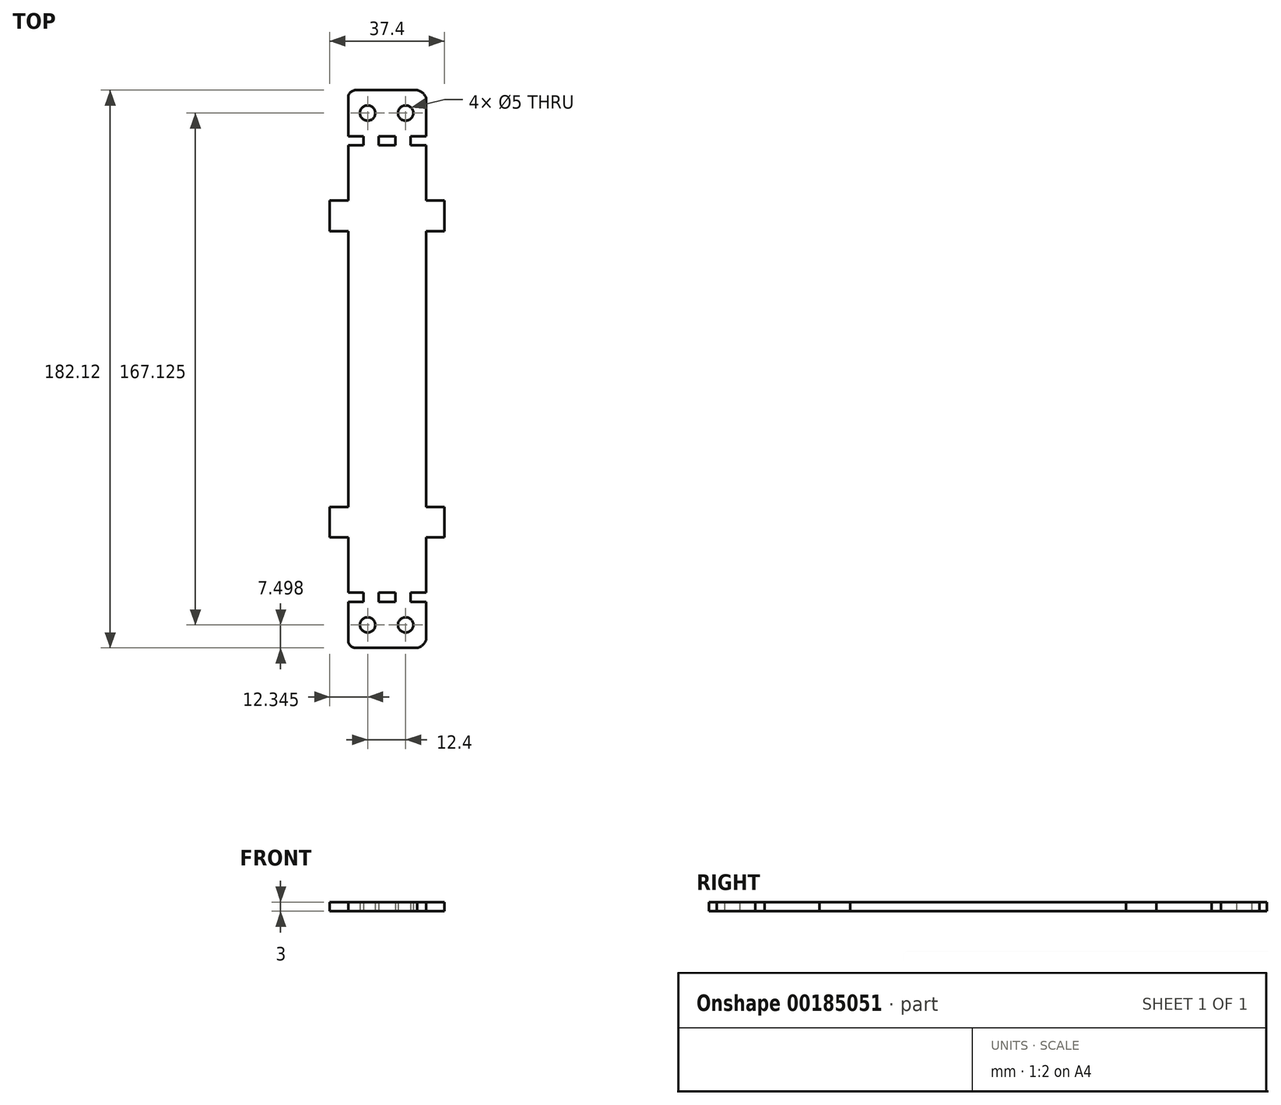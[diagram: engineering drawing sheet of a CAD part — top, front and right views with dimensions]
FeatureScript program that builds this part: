
annotation { "Feature Type Name" : "Feature", "Feature Type Description" : "" }
export const myFeature = defineFeature(function(context is Context, id is Id, definition is map)
    precondition{}
    {
        {
            var Q0;
            Q0=qCreatedBy(makeId("Top.planeOp"),FACE);
            var sketch = newSketch(context, id + "F0", { "sketchPlane" : qUnion([Q0])});
            skLineSegment(sketch, "E0", {"start": v(0, 91) * mm, "end": v(-10, 91) * mm});
            skLineSegment(sketch, "E1", {"start": v(-12.5, 76) * mm, "end": v(-9.5, 76) * mm});
            skLineSegment(sketch, "E2", {"start": v(-9.5, 76) * mm, "end": v(-9.5, 73) * mm});
            skLineSegment(sketch, "E3", {"start": v(-9.5, 73) * mm, "end": v(-12.5, 73) * mm});
            skLineSegment(sketch, "E4", {"start": v(-12.5, 88.5) * mm, "end": v(-12.5, 76) * mm});
            skLineSegment(sketch, "E5", {"start": v(0, 76) * mm, "end": v(-3, 76) * mm});
            skLineSegment(sketch, "E6", {"start": v(-3, 76) * mm, "end": v(-3, 73) * mm});
            skLineSegment(sketch, "E7", {"start": v(-3, 73) * mm, "end": v(0, 73) * mm});
            skCircle(sketch, "E8", {"center": v(-6.25, 83.5) * mm, "radius": 2.5 * mm});
            skPoint(sketch, "E8.centerSnap0", {"position": v(-12.5, 83.5) * mm});
            skPoint(sketch, "E8.centerSnap1", {"position": v(-6.25, 91) * mm});
            skPoint(sketch, "E9.visualSharp", {"position": v(-12.5, 91) * mm});
            skArc(sketch, "E9.filletArc", {"start": v(-10, 91) * mm, "mid": v(-11.77, 90.27) * mm, "end": v(-12.5, 88.5) * mm});
            skLineSegment(sketch, "E10", {"start": v(-12.5, 35) * mm, "end": v(-17.84, 35) * mm});
            skLineSegment(sketch, "E11", {"start": v(-18.5, 35.66) * mm, "end": v(-18.5, 44.34) * mm});
            skLineSegment(sketch, "E12", {"start": v(-17.84, 45) * mm, "end": v(-12.5, 45) * mm});
            skLineSegment(sketch, "E13", {"start": v(-12.5, 45) * mm, "end": v(-12.5, 73) * mm});
            skLineSegment(sketch, "E14", {"start": v(-12.5, 35) * mm, "end": v(-12.5, 0) * mm});
            skPoint(sketch, "E15.visualSharp", {"position": v(-18.5, 45) * mm});
            skArc(sketch, "E15.filletArc", {"start": v(-17.84, 45) * mm, "mid": v(-18.3, 44.8) * mm, "end": v(-18.5, 44.34) * mm});
            skPoint(sketch, "E16.visualSharp", {"position": v(-18.5, 35) * mm});
            skArc(sketch, "E16.filletArc", {"start": v(-18.5, 35.66) * mm, "mid": v(-18.3, 35.2) * mm, "end": v(-17.84, 35) * mm});
            skArc(sketch, "E17.MirrorCS", {"start": v(10, 91) * mm, "mid": v(11.77, 90.27) * mm, "end": v(12.5, 88.5) * mm});
            skLineSegment(sketch, "E18.MirrorCS", {"start": v(9.5, 76) * mm, "end": v(9.5, 73) * mm});
            skLineSegment(sketch, "E19.MirrorCS", {"start": v(9.5, 73) * mm, "end": v(12.5, 73) * mm});
            skLineSegment(sketch, "E20.MirrorCS", {"start": v(3, 76) * mm, "end": v(3, 73) * mm});
            skLineSegment(sketch, "E21.MirrorCS", {"start": v(12.5, 76) * mm, "end": v(9.5, 76) * mm});
            skLineSegment(sketch, "E22.MirrorCS", {"start": v(12.5, 35) * mm, "end": v(17.84, 35) * mm});
            skLineSegment(sketch, "E23.MirrorCS", {"start": v(17.84, 45) * mm, "end": v(12.5, 45) * mm});
            skLineSegment(sketch, "E24.MirrorCS", {"start": v(3, 73) * mm, "end": v(0, 73) * mm});
            skLineSegment(sketch, "E25.MirrorCS", {"start": v(0, 76) * mm, "end": v(3, 76) * mm});
            skPoint(sketch, "E26.MirrorP", {"position": v(6.25, 91) * mm});
            skCircle(sketch, "E27.MirrorC", {"center": v(6.25, 83.5) * mm, "radius": 2.5 * mm});
            skLineSegment(sketch, "E28.MirrorCS", {"start": v(0, 91) * mm, "end": v(10, 91) * mm});
            skLineSegment(sketch, "E29.MirrorCS", {"start": v(12.5, 45) * mm, "end": v(12.5, 73) * mm});
            skLineSegment(sketch, "E30.MirrorCS", {"start": v(12.5, 35) * mm, "end": v(12.5, 0) * mm});
            skLineSegment(sketch, "E31.MirrorCS", {"start": v(12.5, 88.5) * mm, "end": v(12.5, 76) * mm});
            skArc(sketch, "E32.MirrorCS", {"start": v(-17.84, -45) * mm, "mid": v(-18.3, -44.8) * mm, "end": v(-18.5, -44.34) * mm});
            skArc(sketch, "E33.MirrorCS", {"start": v(17.84, -45) * mm, "mid": v(18.3, -44.8) * mm, "end": v(18.5, -44.34) * mm});
            skArc(sketch, "E34.MirrorCS", {"start": v(-18.5, -35.66) * mm, "mid": v(-18.3, -35.2) * mm, "end": v(-17.84, -35) * mm});
            skArc(sketch, "E35.MirrorCS", {"start": v(-10, -91) * mm, "mid": v(-11.77, -90.27) * mm, "end": v(-12.5, -88.5) * mm});
            skArc(sketch, "E36.MirrorCS", {"start": v(32.1, -123.66) * mm, "mid": v(31.9, -123.2) * mm, "end": v(31.44, -123) * mm});
            skArc(sketch, "E37.MirrorCS", {"start": v(10, -91) * mm, "mid": v(11.77, -90.27) * mm, "end": v(12.5, -88.5) * mm});
            skLineSegment(sketch, "E38.MirrorCS", {"start": v(-17.84, -45) * mm, "end": v(-12.5, -45) * mm});
            skLineSegment(sketch, "E39.MirrorCS", {"start": v(9.5, -76) * mm, "end": v(9.5, -73) * mm});
            skLineSegment(sketch, "E40.MirrorCS", {"start": v(12.5, -76) * mm, "end": v(9.5, -76) * mm});
            skLineSegment(sketch, "E41.MirrorCS", {"start": v(3, -73) * mm, "end": v(0, -73) * mm});
            skLineSegment(sketch, "E42.MirrorCS", {"start": v(12.5, -35) * mm, "end": v(17.84, -35) * mm});
            skLineSegment(sketch, "E43.MirrorCS", {"start": v(3, -76) * mm, "end": v(3, -73) * mm});
            skLineSegment(sketch, "E44.MirrorCS", {"start": v(17.84, -45) * mm, "end": v(12.5, -45) * mm});
            skLineSegment(sketch, "E45.MirrorCS", {"start": v(-9.5, -73) * mm, "end": v(-12.5, -73) * mm});
            skLineSegment(sketch, "E46.MirrorCS", {"start": v(0, -76) * mm, "end": v(3, -76) * mm});
            skLineSegment(sketch, "E47.MirrorCS", {"start": v(-12.5, -76) * mm, "end": v(-9.5, -76) * mm});
            skLineSegment(sketch, "E48.MirrorCS", {"start": v(-9.5, -76) * mm, "end": v(-9.5, -73) * mm});
            skLineSegment(sketch, "E49.MirrorCS", {"start": v(0, -76) * mm, "end": v(-3, -76) * mm});
            skLineSegment(sketch, "E50.MirrorCS", {"start": v(-3, -76) * mm, "end": v(-3, -73) * mm});
            skLineSegment(sketch, "E51.MirrorCS", {"start": v(-3, -73) * mm, "end": v(0, -73) * mm});
            skLineSegment(sketch, "E52.MirrorCS", {"start": v(9.5, -73) * mm, "end": v(12.5, -73) * mm});
            skLineSegment(sketch, "E53.MirrorCS", {"start": v(-12.5, -35) * mm, "end": v(-17.84, -35) * mm});
            skLineSegment(sketch, "E54.MirrorCS", {"start": v(0, -91) * mm, "end": v(10, -91) * mm});
            skLineSegment(sketch, "E55.MirrorCS", {"start": v(-18.5, -35.66) * mm, "end": v(-18.5, -44.34) * mm});
            skLineSegment(sketch, "E56.MirrorCS", {"start": v(12.5, -88.5) * mm, "end": v(12.5, -76) * mm});
            skPoint(sketch, "E57.MirrorP", {"position": v(-12.5, -83.5) * mm});
            skPoint(sketch, "E58.MirrorP", {"position": v(-12.5, -91) * mm});
            skLineSegment(sketch, "E59.MirrorCS", {"start": v(18.5, -35.66) * mm, "end": v(18.5, -44.34) * mm});
            skPoint(sketch, "E60.MirrorP", {"position": v(-18.5, -45) * mm});
            skPoint(sketch, "E61.MirrorP", {"position": v(12.5, -91) * mm});
            skPoint(sketch, "E62.MirrorP", {"position": v(-6.25, -91) * mm});
            skCircle(sketch, "E63.MirrorC", {"center": v(6.25, -83.5) * mm, "radius": 2.5 * mm});
            skLineSegment(sketch, "E64.MirrorCS", {"start": v(-12.5, -88.5) * mm, "end": v(-12.5, -76) * mm});
            skLineSegment(sketch, "E65.MirrorCS", {"start": v(0, -91) * mm, "end": v(-10, -91) * mm});
            skLineSegment(sketch, "E66.MirrorCS", {"start": v(-12.5, -35) * mm, "end": v(-12.5, 0) * mm});
            skPoint(sketch, "E67.MirrorP", {"position": v(12.5, -83.5) * mm});
            skCircle(sketch, "E68.MirrorC", {"center": v(-6.25, -83.5) * mm, "radius": 2.5 * mm});
            skLineSegment(sketch, "E69.MirrorCS", {"start": v(-12.5, -45) * mm, "end": v(-12.5, -73) * mm});
            skLineSegment(sketch, "E70.MirrorCS", {"start": v(12.5, -35) * mm, "end": v(12.5, 0) * mm});
            skPoint(sketch, "E71.MirrorP", {"position": v(-18.5, -35) * mm});
            skLineSegment(sketch, "E72.MirrorCS", {"start": v(12.5, -45) * mm, "end": v(12.5, -73) * mm});
            skPoint(sketch, "E73.MirrorP", {"position": v(32.1, -123) * mm});
            skPoint(sketch, "E74.MirrorP", {"position": v(6.25, -91) * mm});
            skLineSegment(sketch, "E75", {"start": v(35.48, 76) * mm, "end": v(40.48, 76) * mm});
            skLineSegment(sketch, "E76", {"start": v(40.48, 76) * mm, "end": v(40.48, 73) * mm});
            skLineSegment(sketch, "E77", {"start": v(40.48, 73) * mm, "end": v(35.48, 73) * mm});
            skLineSegment(sketch, "E78", {"start": v(35.48, 88.56) * mm, "end": v(35.48, 76) * mm});
            skLineSegment(sketch, "E79", {"start": v(45.48, 76) * mm, "end": v(45.48, 73) * mm});
            skCircle(sketch, "E80", {"center": v(41.83, 83.56) * mm, "radius": 2.5 * mm});
            skPoint(sketch, "E80.centerSnap0", {"position": v(35.48, 83.56) * mm});
            skPoint(sketch, "E80.centerSnap1", {"position": v(41.83, 91.06) * mm});
            skPoint(sketch, "E81.visualSharp", {"position": v(35.48, 91.13) * mm});
            skArc(sketch, "E81.filletArc", {"start": v(37.98, 91.06) * mm, "mid": v(36.2, 90.33) * mm, "end": v(35.48, 88.56) * mm});
            skLineSegment(sketch, "E82", {"start": v(35.48, 45) * mm, "end": v(29.48, 45) * mm});
            skLineSegment(sketch, "E83", {"start": v(29.48, 55) * mm, "end": v(35.48, 55) * mm});
            skLineSegment(sketch, "E84", {"start": v(35.48, 55) * mm, "end": v(35.48, 73) * mm});
            skLineSegment(sketch, "E85", {"start": v(35.48, 45) * mm, "end": v(35.48, 0) * mm});
            skArc(sketch, "E86.MirrorCS", {"start": v(57.98, 91.06) * mm, "mid": v(59.74, 90.18) * mm, "end": v(60.88, 88.56) * mm});
            skLineSegment(sketch, "E87.MirrorCS", {"start": v(55.88, 76) * mm, "end": v(55.88, 73) * mm});
            skLineSegment(sketch, "E88.MirrorCS", {"start": v(55.88, 73) * mm, "end": v(60.88, 73) * mm});
            skLineSegment(sketch, "E89.MirrorCS", {"start": v(50.88, 76) * mm, "end": v(50.88, 73) * mm});
            skLineSegment(sketch, "E90.MirrorCS", {"start": v(60.88, 76) * mm, "end": v(55.88, 76) * mm});
            skLineSegment(sketch, "E91.MirrorCS", {"start": v(60.88, 45) * mm, "end": v(66.88, 45) * mm});
            skLineSegment(sketch, "E92.MirrorCS", {"start": v(66.88, 55) * mm, "end": v(60.88, 55) * mm});
            skPoint(sketch, "E93.MirrorP", {"position": v(54.23, 91.06) * mm});
            skCircle(sketch, "E94.MirrorC", {"center": v(54.23, 83.56) * mm, "radius": 2.5 * mm});
            skPoint(sketch, "E95.MirrorP", {"position": v(60.48, 91.06) * mm});
            skPoint(sketch, "E96.MirrorP", {"position": v(60.48, 83.56) * mm});
            skLineSegment(sketch, "E97.MirrorCS", {"start": v(60.88, 55) * mm, "end": v(60.88, 73) * mm});
            skLineSegment(sketch, "E98.MirrorCS", {"start": v(60.88, 45) * mm, "end": v(60.88, 0) * mm});
            skLineSegment(sketch, "E99.MirrorCS", {"start": v(60.88, 88.56) * mm, "end": v(60.88, 76) * mm});
            skLineSegment(sketch, "E100", {"start": v(37.98, 91.06) * mm, "end": v(57.98, 91.06) * mm});
            skLineSegment(sketch, "E101", {"start": v(45.48, 76) * mm, "end": v(50.88, 76) * mm});
            skLineSegment(sketch, "E102", {"start": v(50.88, 73) * mm, "end": v(45.48, 73) * mm});
            skLineSegment(sketch, "E103", {"start": v(17.84, 45) * mm, "end": v(17.84, 35) * mm});
            skLineSegment(sketch, "E104", {"start": v(29.48, 55) * mm, "end": v(29.48, 45) * mm});
            skLineSegment(sketch, "E105", {"start": v(66.88, 55) * mm, "end": v(66.88, 45) * mm});
            skArc(sketch, "E106.MirrorCS", {"start": v(37.98, -91.06) * mm, "mid": v(36.2, -90.33) * mm, "end": v(35.48, -88.56) * mm});
            skArc(sketch, "E107.MirrorCS", {"start": v(57.98, -91.06) * mm, "mid": v(59.74, -90.18) * mm, "end": v(60.88, -88.56) * mm});
            skLineSegment(sketch, "E108.MirrorCS", {"start": v(45.48, -76) * mm, "end": v(45.48, -73) * mm});
            skLineSegment(sketch, "E109.MirrorCS", {"start": v(55.88, -76) * mm, "end": v(55.88, -73) * mm});
            skLineSegment(sketch, "E110.MirrorCS", {"start": v(66.88, -55) * mm, "end": v(60.88, -55) * mm});
            skLineSegment(sketch, "E111.MirrorCS", {"start": v(35.48, -76) * mm, "end": v(40.48, -76) * mm});
            skLineSegment(sketch, "E112.MirrorCS", {"start": v(55.88, -73) * mm, "end": v(60.88, -73) * mm});
            skLineSegment(sketch, "E113.MirrorCS", {"start": v(35.48, -45) * mm, "end": v(29.48, -45) * mm});
            skLineSegment(sketch, "E114.MirrorCS", {"start": v(45.48, -76) * mm, "end": v(50.88, -76) * mm});
            skLineSegment(sketch, "E115.MirrorCS", {"start": v(60.88, -76) * mm, "end": v(55.88, -76) * mm});
            skLineSegment(sketch, "E116.MirrorCS", {"start": v(50.88, -76) * mm, "end": v(50.88, -73) * mm});
            skLineSegment(sketch, "E117.MirrorCS", {"start": v(29.48, -55) * mm, "end": v(35.48, -55) * mm});
            skLineSegment(sketch, "E118.MirrorCS", {"start": v(50.88, -73) * mm, "end": v(45.48, -73) * mm});
            skLineSegment(sketch, "E119.MirrorCS", {"start": v(40.48, -73) * mm, "end": v(35.48, -73) * mm});
            skLineSegment(sketch, "E120.MirrorCS", {"start": v(40.48, -76) * mm, "end": v(40.48, -73) * mm});
            skLineSegment(sketch, "E121.MirrorCS", {"start": v(60.88, -45) * mm, "end": v(66.88, -45) * mm});
            skLineSegment(sketch, "E122.MirrorCS", {"start": v(60.88, -88.56) * mm, "end": v(60.88, -76) * mm});
            skCircle(sketch, "E123.MirrorC", {"center": v(54.23, -83.56) * mm, "radius": 2.5 * mm});
            skLineSegment(sketch, "E124.MirrorCS", {"start": v(35.48, -88.56) * mm, "end": v(35.48, -76) * mm});
            skPoint(sketch, "E125.MirrorP", {"position": v(35.48, -91.13) * mm});
            skLineSegment(sketch, "E126.MirrorCS", {"start": v(29.48, -55) * mm, "end": v(29.48, -45) * mm});
            skPoint(sketch, "E127.MirrorP", {"position": v(41.83, -91.06) * mm});
            skPoint(sketch, "E128.MirrorP", {"position": v(60.48, -83.56) * mm});
            skLineSegment(sketch, "E129.MirrorCS", {"start": v(60.88, -45) * mm, "end": v(60.88, 0) * mm});
            skLineSegment(sketch, "E130.MirrorCS", {"start": v(37.98, -91.06) * mm, "end": v(57.98, -91.06) * mm});
            skCircle(sketch, "E131.MirrorC", {"center": v(41.83, -83.56) * mm, "radius": 2.5 * mm});
            skLineSegment(sketch, "E132.MirrorCS", {"start": v(35.48, -55) * mm, "end": v(35.48, -73) * mm});
            skPoint(sketch, "E133.MirrorP", {"position": v(35.48, -83.56) * mm});
            skPoint(sketch, "E134.MirrorP", {"position": v(60.48, -91.06) * mm});
            skLineSegment(sketch, "E135.MirrorCS", {"start": v(60.88, -55) * mm, "end": v(60.88, -73) * mm});
            skLineSegment(sketch, "E136.MirrorCS", {"start": v(35.48, -45) * mm, "end": v(35.48, 0) * mm});
            skPoint(sketch, "E137.MirrorP", {"position": v(54.23, -91.06) * mm});
            skLineSegment(sketch, "E138.MirrorCS", {"start": v(66.88, -55) * mm, "end": v(66.88, -45) * mm});
            skSolve(sketch);
        }
        {
            var Q0;
            Q0=makeQuery(id+"F0.imprint","IMPRINT",FACE,{"disambiguationData":[TD([[makeQuery(id+"F0.imprint","IMPRINT",EDGE,{"derivedFrom":sQuery(id+"F0.wireOp",EDGE,"E75")}),1.0]])]});
            extrude(context, id + "F1", {"entities" : qUnion([Q0]), "depth" : 3 * mm});
        }
    });
